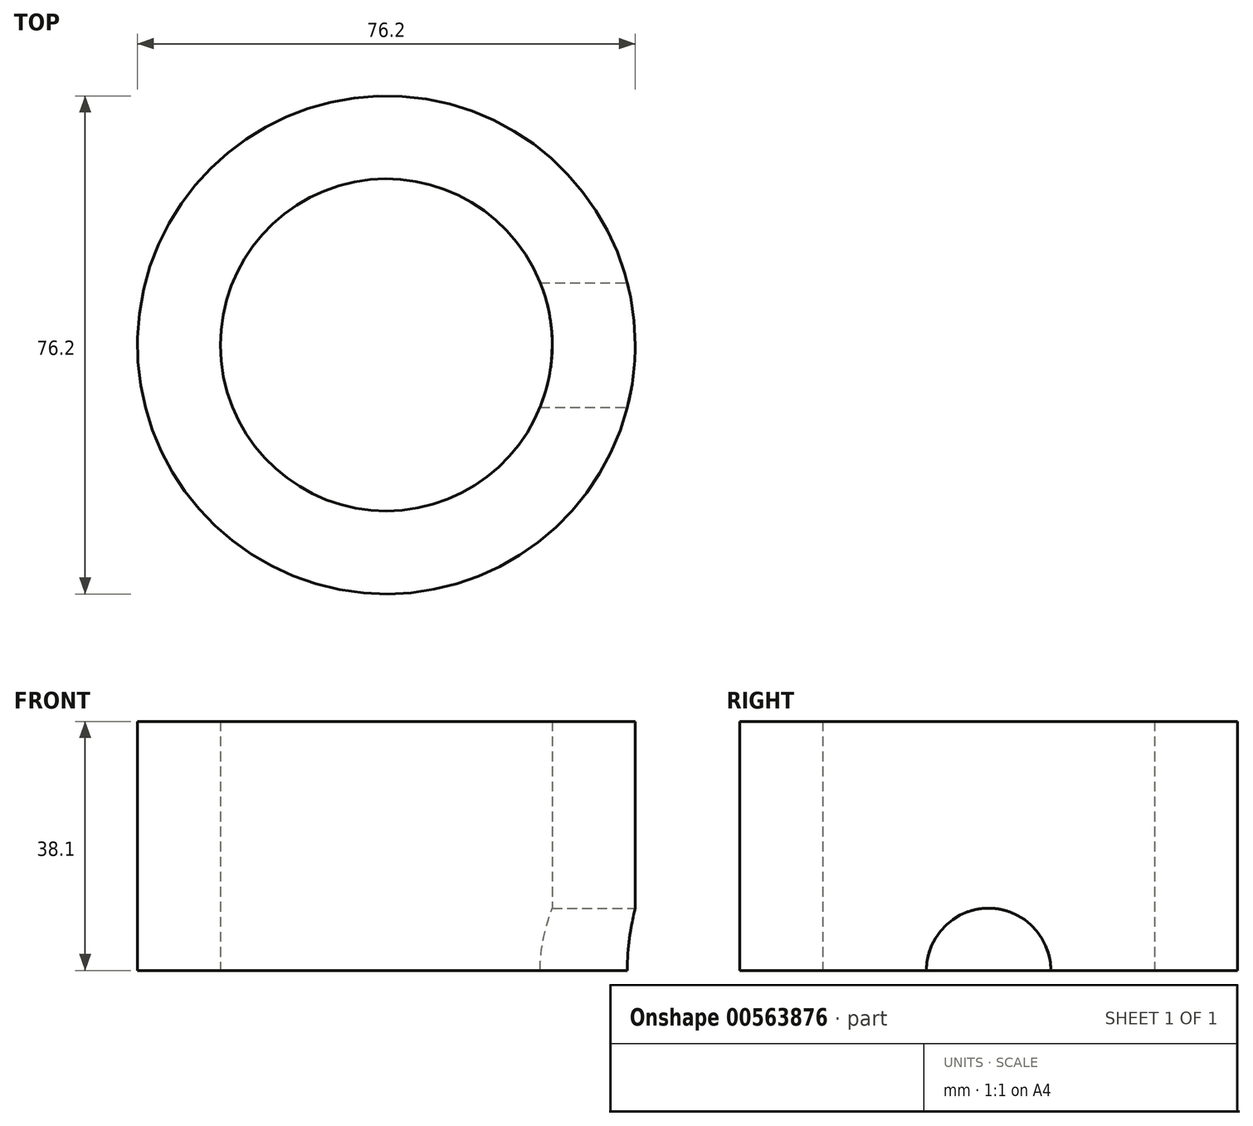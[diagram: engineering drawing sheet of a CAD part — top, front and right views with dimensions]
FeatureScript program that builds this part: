
annotation { "Feature Type Name" : "Feature", "Feature Type Description" : "" }
export const myFeature = defineFeature(function(context is Context, id is Id, definition is map)
    precondition{}
    {
        {
            var Q0;
            Q0=qCreatedBy(makeId("Top.planeOp"),FACE);
            var sketch = newSketch(context, id + "F0", { "sketchPlane" : qUnion([Q0])});
            skCircle(sketch, "E0", {"center": v(0, 0) * mm, "radius": 38.1 * mm});
            skCircle(sketch, "E1", {"center": v(0, 0) * mm, "radius": 25.4 * mm});
            skSolve(sketch);
        }
        {
            var Q0;
            Q0=makeQuery(id+"F0.imprint","IMPRINT",FACE,{"disambiguationData":[TD([[makeQuery(id+"F0.imprint","IMPRINT",EDGE,{"derivedFrom":sQuery(id+"F0.wireOp",EDGE,"E0")}),1.0]])]});
            extrude(context, id + "F1", {"entities" : qUnion([Q0]), "depth" : 38.1 * mm, "offsetDistance" : 25.4 * mm});
        }
        {
            var Q0;
            Q0=qCreatedBy(makeId("Right.planeOp"),FACE);
            cPlane(context, id + "F2", {"entities" : qUnion([Q0]), "cplaneType" : CPlaneType.OFFSET, "offset" : 38.1 * mm, "width" : 152.4 * mm, "height" : 152.4 * mm});
        }
        {
            var Q0;
            Q0=qCreatedBy(id+"F2.planeOp",FACE);
            var sketch = newSketch(context, id + "F3", { "sketchPlane" : qUnion([Q0])});
            skPoint(sketch, "E2", {"position": v(0, 0) * mm});
            skSolve(sketch);
        }
        {
            var Q0;
            Q0=sQuery(id+"F3.wireOp",VERTEX,"E2");
            var Q1;
            Q1=makeQuery(id+"F1.opExtrude","SWEPT_BODY",BODY,{"disambiguationData":[OSD([sQuery(id+"F0.wireOp",EDGE,"E0"),sQuery(id+"F0.wireOp",EDGE,"E1")])]});
            hole(context, id + "F4", {"style" : HoleStyle.SIMPLE, "endStyle" : HoleEndStyle.BLIND, "holeDiameter" : 19.05 * mm, "holeDepth" : 25.4 * mm, "isTappedThrough" : true, "tappedDepth" : 12.7 * mm, "tapClearance" : 3, "locations" : qUnion([Q0]), "scope" : qUnion([Q1])});
        }
    });
